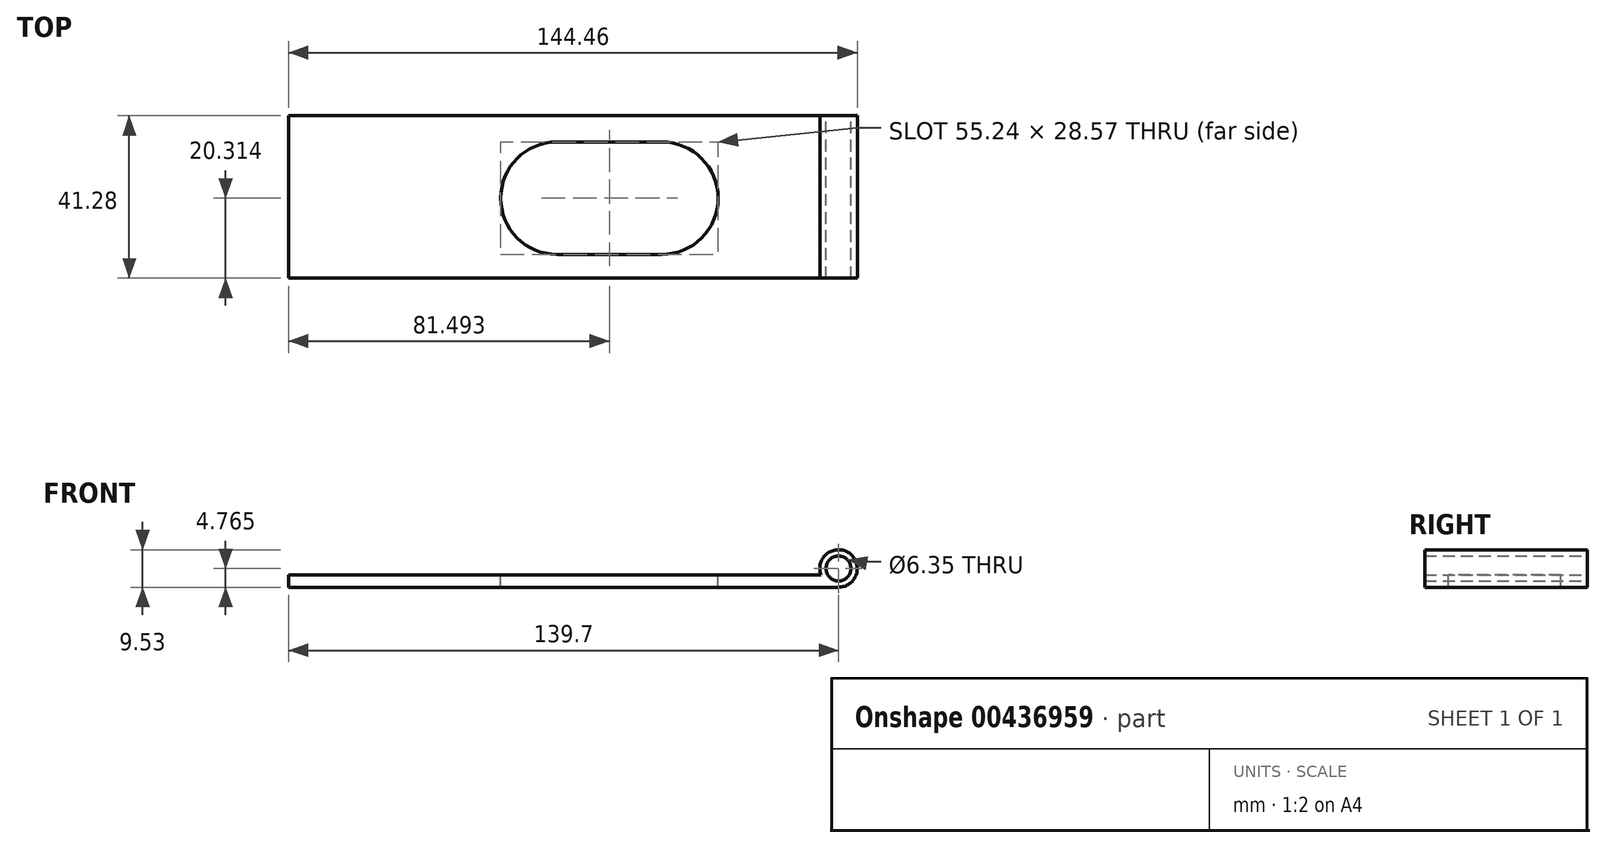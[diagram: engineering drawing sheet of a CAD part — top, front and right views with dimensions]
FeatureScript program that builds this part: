
annotation { "Feature Type Name" : "Feature", "Feature Type Description" : "" }
export const myFeature = defineFeature(function(context is Context, id is Id, definition is map)
    precondition{}
    {
        {
            var Q0;
            Q0=qCreatedBy(makeId("Front.planeOp"),FACE);
            var sketch = newSketch(context, id + "F0", { "sketchPlane" : qUnion([Q0])});
            skLineSegment(sketch, "E0", {"start": v(95.25, -1.59) * mm, "end": v(-44.45, -1.59) * mm});
            skLineSegment(sketch, "E1", {"start": v(-44.45, -1.59) * mm, "end": v(-44.45, 1.59) * mm});
            skLineSegment(sketch, "E2", {"start": v(-44.45, 1.59) * mm, "end": v(90.76, 1.59) * mm});
            skArc(sketch, "E3", {"start": v(95.25, -1.59) * mm, "mid": v(98, 7.06) * mm, "end": v(90.76, 1.59) * mm});
            skCircle(sketch, "E4", {"center": v(95.25, 3.18) * mm, "radius": 3.18 * mm});
            skSolve(sketch);
        }
        {
            var Q0;
            Q0=qSketchRegion(id+"F0",true);
            extrude(context, id + "F1", {"entities" : qUnion([Q0]), "depth" : 41.27 * mm});
        }
        {
            var Q0;
            Q0=makeQuery(id+"F1.opExtrude","SWEPT_FACE",FACE,{"disambiguationData":[OSD([sQuery(id+"F0.wireOp",EDGE,"E2")])]});
            var sketch = newSketch(context, id + "F2", { "sketchPlane" : qUnion([Q0])});
            skArc(sketch, "E5", {"start": v(50.37, -35.25) * mm, "mid": v(64.66, -20.97) * mm, "end": v(50.37, -6.68) * mm});
            skPoint(sketch, "E6", {"position": v(94.82, -15.88) * mm});
            skArc(sketch, "E7", {"start": v(23.71, -6.68) * mm, "mid": v(9.42, -20.97) * mm, "end": v(23.71, -35.25) * mm});
            skLineSegment(sketch, "E8", {"start": v(23.71, -6.68) * mm, "end": v(50.37, -6.68) * mm});
            skLineSegment(sketch, "E9", {"start": v(23.71, -35.25) * mm, "end": v(50.37, -35.25) * mm});
            skSolve(sketch);
        }
        {
            var Q0;
            Q0 = qSketchRegion(id + "F2", true);
            extrude(context, id + "F3", {"entities" : qUnion([Q0]), "operationType" : NewBodyOperationType.REMOVE, "endBound" : BoundingType.UP_TO_NEXT, "oppositeDirection" : true, "depth" : 25.4 * mm});
        }
    });
